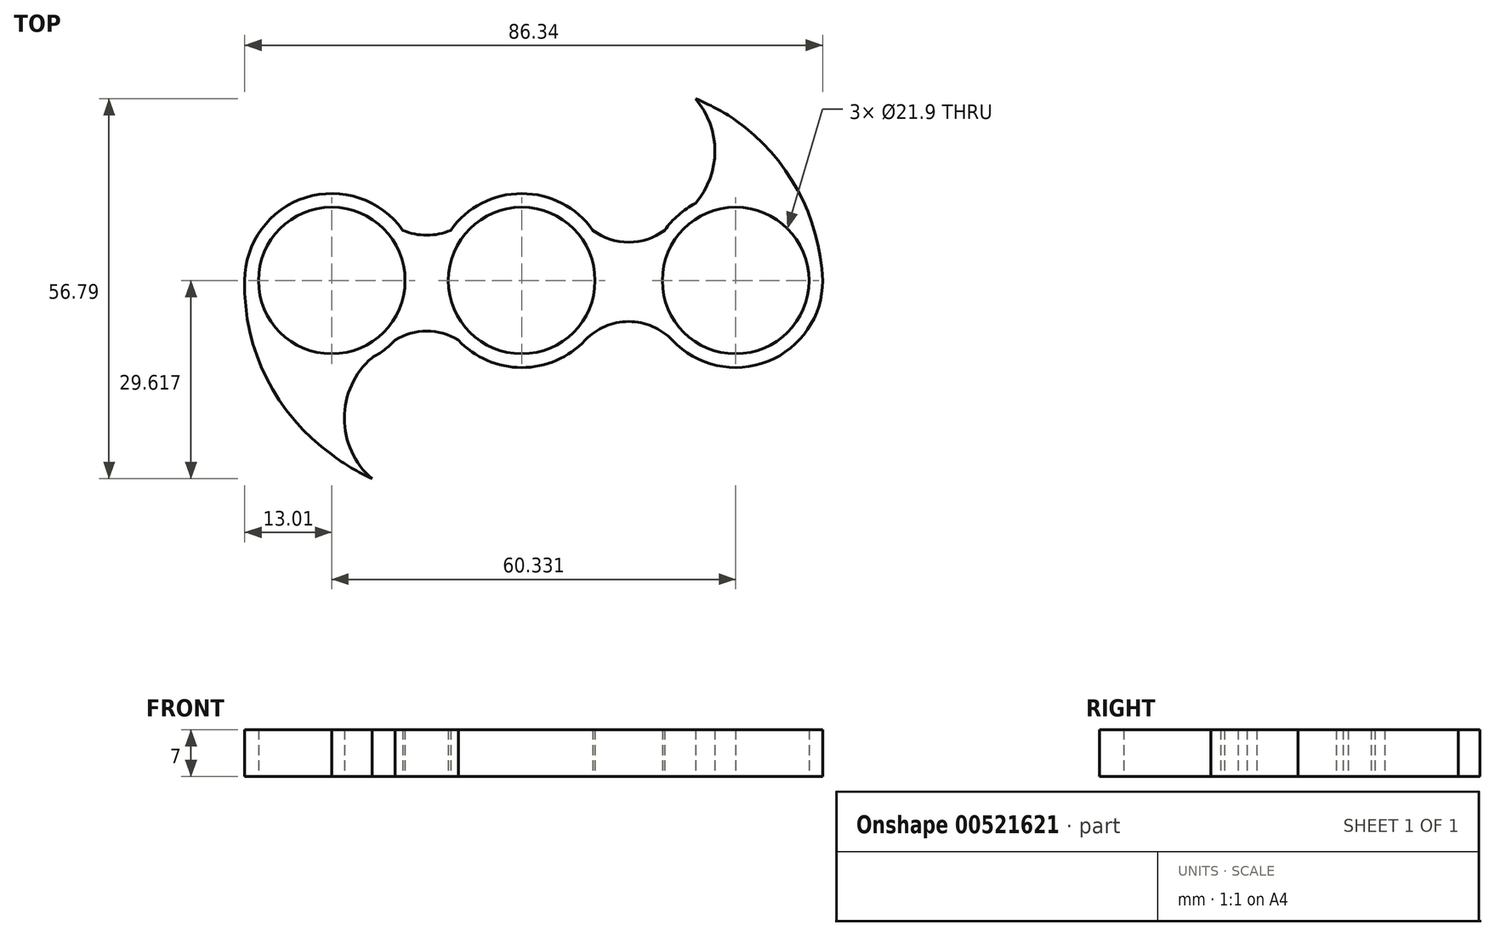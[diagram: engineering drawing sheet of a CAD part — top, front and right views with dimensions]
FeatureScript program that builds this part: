
annotation { "Feature Type Name" : "Feature", "Feature Type Description" : "" }
export const myFeature = defineFeature(function(context is Context, id is Id, definition is map)
    precondition{}
    {
        {
            var Q0;
            Q0=qCreatedBy(makeId("Top.planeOp"),FACE);
            var sketch = newSketch(context, id + "F0", { "sketchPlane" : qUnion([Q0])});
            skCircle(sketch, "E0", {"center": v(-1.64, 2.16) * mm, "radius": 10.95 * mm});
            skCircle(sketch, "E1", {"center": v(-30.02, 2.16) * mm, "radius": 10.95 * mm});
            skCircle(sketch, "E2", {"center": v(30.31, 2.16) * mm, "radius": 10.95 * mm});
            skCircle(sketch, "E3", {"center": v(-30.02, 2.16) * mm, "radius": 13 * mm});
            skCircle(sketch, "E4", {"center": v(-1.64, 2.16) * mm, "radius": 13 * mm});
            skCircle(sketch, "E5", {"center": v(30.31, 2.16) * mm, "radius": 13 * mm});
            skLineSegment(sketch, "E6", {"start": v(-31.2, 6.3) * mm, "end": v(-31.2, 13.04) * mm});
            skLineSegment(sketch, "E7", {"start": v(-31.2, -4.78) * mm, "end": v(-31.2, -8.73) * mm});
            skArc(sketch, "E8", {"start": v(-19.41, 9.67) * mm, "mid": v(-15.83, 8.93) * mm, "end": v(-12.25, 9.67) * mm});
            skPoint(sketch, "E8.startSnap0", {"position": v(-31.2, 9.67) * mm});
            skPoint(sketch, "E8.endSnap0", {"position": v(-31.2, 9.67) * mm});
            skArc(sketch, "E9", {"start": v(-11.1, -6.75) * mm, "mid": v(-15.83, -5.41) * mm, "end": v(-20.55, -6.75) * mm});
            skPoint(sketch, "E9.startSnap0", {"position": v(-31.2, -6.75) * mm});
            skPoint(sketch, "E9.endSnap0", {"position": v(-31.2, -6.75) * mm});
            skArc(sketch, "E10", {"start": v(8.97, 9.67) * mm, "mid": v(14.34, 7.9) * mm, "end": v(19.7, 9.67) * mm});
            skArc(sketch, "E11", {"start": v(20.84, -6.75) * mm, "mid": v(14.34, -3.97) * mm, "end": v(7.83, -6.75) * mm});
            skArc(sketch, "E12", {"start": v(-43.02, 2.16) * mm, "mid": v(-39.76, -12.46) * mm, "end": v(-30.02, -23.84) * mm});
            skArc(sketch, "E13", {"start": v(-30.02, -23.84) * mm, "mid": v(-27.12, -25.82) * mm, "end": v(-24.02, -27.46) * mm});
            skArc(sketch, "E14", {"start": v(-24.02, -9.38) * mm, "mid": v(-28.13, -18.42) * mm, "end": v(-24.02, -27.46) * mm});
            skPoint(sketch, "E15.startSnap0", {"position": v(-22.43, 2.45) * mm});
            skPoint(sketch, "E15.endSnap0", {"position": v(-22.43, 2.45) * mm});
            skArc(sketch, "E16", {"start": v(43.31, 2.16) * mm, "mid": v(39.59, 15.64) * mm, "end": v(30.31, 26.12) * mm});
            skArc(sketch, "E17", {"start": v(30.31, 26.12) * mm, "mid": v(27.4, 27.89) * mm, "end": v(24.31, 29.33) * mm});
            skArc(sketch, "E18", {"start": v(24.31, 13.69) * mm, "mid": v(27.2, 21.5) * mm, "end": v(24.31, 29.33) * mm});
            skSolve(sketch);
        }
        {
            var Q0;
            {var subQ4=sQuery(id+"F0.wireOp",EDGE,"E1");var subQ5=makeQuery(id+"F0.imprint","IMPRINT",VERTEX,{"disambiguationData":[OD(0.0)],"derivedFrom":subQ4});Q0=makeQuery(id+"F0.imprint","IMPRINT",FACE,{"disambiguationData":[TD([[makeQuery(id+"F0.imprint","IMPRINT",EDGE,{"disambiguationData":[TD([[subQ5,-1.0]])],"derivedFrom":subQ4}),-1.0]])]});}
            var Q1;
            {var subQ0=sQuery(id+"F0.wireOp",EDGE,"E12");Q1=makeQuery(id+"F0.imprint","IMPRINT",FACE,{"disambiguationData":[TD([[makeQuery(id+"F0.imprint","IMPRINT",EDGE,{"derivedFrom":subQ0}),1.0]])]});}
            var Q2;
            {var subQ0=sQuery(id+"F0.wireOp",EDGE,"E8");Q2=makeQuery(id+"F0.imprint","IMPRINT",FACE,{"disambiguationData":[TD([[makeQuery(id+"F0.imprint","IMPRINT",EDGE,{"derivedFrom":subQ0}),-1.0]])]});}
            var Q3;
            Q3=makeQuery(id+"F0.imprint","IMPRINT",FACE,{"disambiguationData":[TD([[makeQuery(id+"F0.imprint","IMPRINT",EDGE,{"derivedFrom":sQuery(id+"F0.wireOp",EDGE,"E0")}),-1.0]])]});
            var Q4;
            {var subQ0=sQuery(id+"F0.wireOp",EDGE,"E10");Q4=makeQuery(id+"F0.imprint","IMPRINT",FACE,{"disambiguationData":[TD([[makeQuery(id+"F0.imprint","IMPRINT",EDGE,{"derivedFrom":subQ0}),-1.0]])]});}
            var Q5;
            Q5=makeQuery(id+"F0.imprint","IMPRINT",FACE,{"disambiguationData":[TD([[makeQuery(id+"F0.imprint","IMPRINT",EDGE,{"derivedFrom":sQuery(id+"F0.wireOp",EDGE,"E2")}),-1.0]])]});
            var Q6;
            {var subQ4=sQuery(id+"F0.wireOp",EDGE,"0a9f47c0-3c6e-40af-b38e-c0c66bdee653");Q6=makeQuery(id+"F0.imprint","IMPRINT",FACE,{"disambiguationData":[TD([[makeQuery(id+"F0.imprint","IMPRINT",EDGE,{"derivedFrom":subQ4}),1.0]])]});}
            var Q7;
            {var subQ4=sQuery(id+"F0.wireOp",EDGE,"E17");Q7=makeQuery(id+"F0.imprint","IMPRINT",FACE,{"disambiguationData":[TD([[makeQuery(id+"F0.imprint","IMPRINT",EDGE,{"derivedFrom":subQ4}),1.0]])]});}
            extrude(context, id + "F1", {"entities" : qUnion([Q0, Q1, Q2, Q3, Q4, Q5, Q6, Q7]), "depth" : 7 * mm, "offsetDistance" : 25 * mm});
        }
    });
